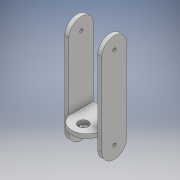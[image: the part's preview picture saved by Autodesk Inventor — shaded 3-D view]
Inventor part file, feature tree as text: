
AUTODESK INVENTOR PART (.ipt)
format: ipt  version: 2018 (Build 220112000, 112)  size: 147,968 bytes
history: native  units: mm
features: extrude x3, sketch x3, fillet x1, hole x1
ambient origin geometry x8: Origin, YZ Plane, XZ Plane, XY Plane, X Axis, Y Axis, Z Axis, Center Point
bodies: Solid1 (feature_tree)
feature tree (8):
  extrude  "Extrusion1"  Depth=40.0mm TaperAngle=0.0deg
  extrude  "Extrusion2"  Depth=15.0mm
  extrude  "Extrusion5"  Depth=5.0mm
  fillet  "Fillet2"  Radius=5.0mm
  hole  "Hole2"  [1 undecoded]
  sketch  "Sketch1"  dims[d0=45.0mm d1=0.0mm d2=40.0mm d3=0.0mm]
  sketch  "Sketch2"  dims[d6=15.0mm d18=100.0mm]
  sketch  "Sketch5"  dims[d19=5.0mm d20=5.0mm d27=5.0mm d28=50.0mm d29=0.0mm d30=18.0mm d31=17.5mm d32=30.0mm d33=12.0mm d34=6.0mm d35=4.0mm d36=2.0mm d37=90.0deg d38=8.0mm d39=20.594885mm d40=4.0mm]
note: 1 required parameter value undecoded (feature->parameter linkage not recoverable at this tier; creation-order binding heuristic only, values carry confidence <= 0.55)
